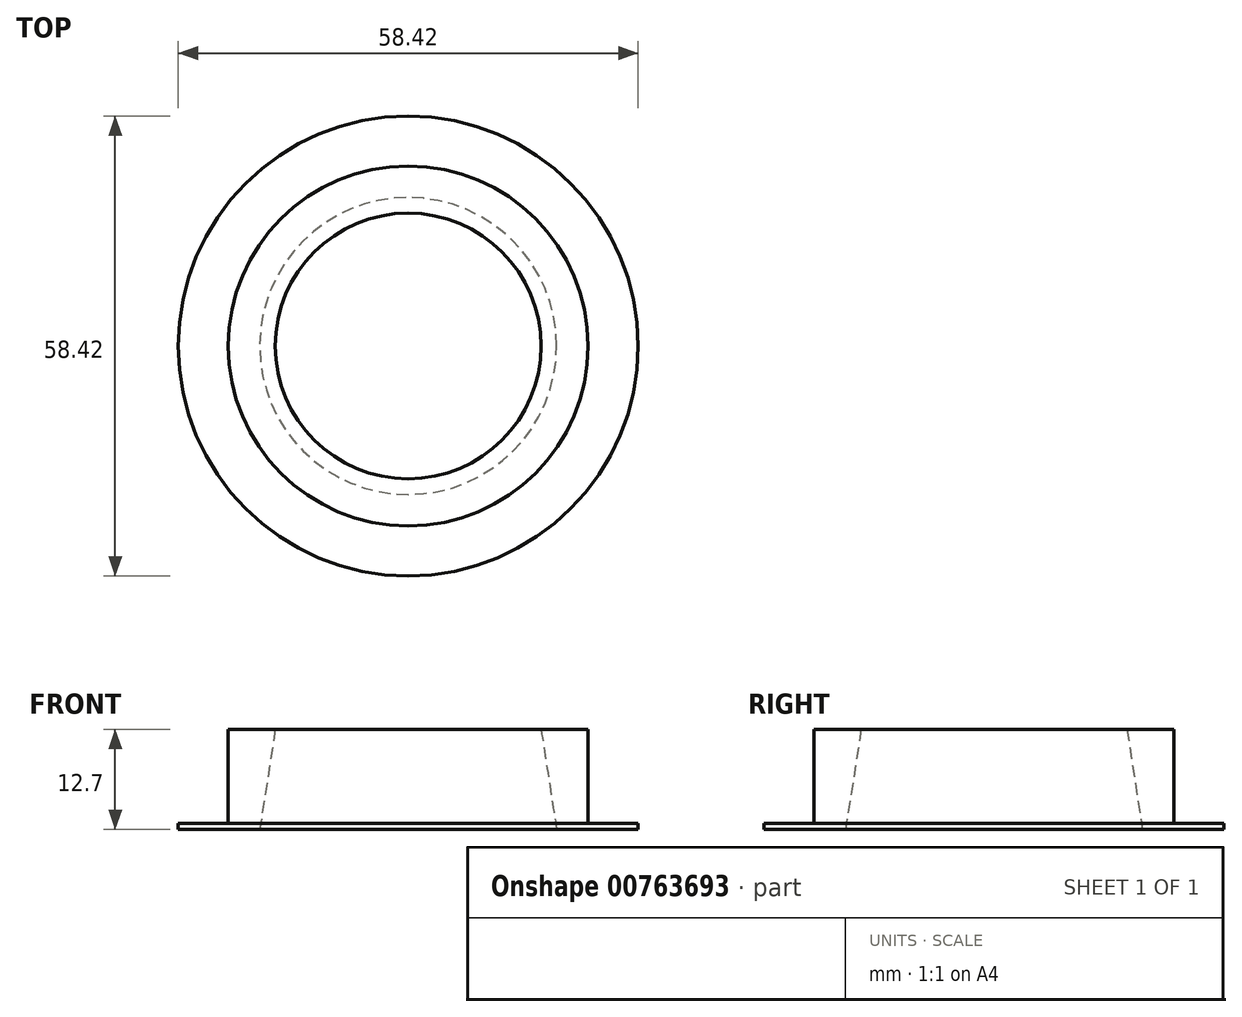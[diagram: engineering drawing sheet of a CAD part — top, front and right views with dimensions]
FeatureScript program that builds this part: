
annotation { "Feature Type Name" : "Feature", "Feature Type Description" : "" }
export const myFeature = defineFeature(function(context is Context, id is Id, definition is map)
    precondition{}
    {
        {
            var Q0;
            Q0=qCreatedBy(makeId("Top.planeOp"),FACE);
            var sketch = newSketch(context, id + "F0", { "sketchPlane" : qUnion([Q0])});
            skCircle(sketch, "E0", {"center": v(0, 0) * mm, "radius": 29.21 * mm});
            skSolve(sketch);
        }
        {
            var Q0;
            Q0 = qSketchRegion(id + "F0", true);
            extrude(context, id + "F1", {"entities" : qUnion([Q0]), "depth" : 0.76 * mm, "offsetDistance" : 25.4 * mm});
        }
        {
            var Q0;
            Q0=makeQuery(id+"F1.opExtrude","CAP_FACE",FACE,{"disambiguationData":[OSD([sQuery(id+"F0.wireOp",EDGE,"E0")])],"isStart":false});
            var sketch = newSketch(context, id + "F2", { "sketchPlane" : qUnion([Q0])});
            skCircle(sketch, "E1", {"center": v(0, 0) * mm, "radius": 22.86 * mm});
            skSolve(sketch);
        }
        {
            var Q0;
            Q0=makeQuery(id+"F2.imprint","IMPRINT",FACE,{"disambiguationData":[TD([[makeQuery(id+"F2.imprint","IMPRINT",EDGE,{"derivedFrom":sQuery(id+"F2.wireOp",EDGE,"E1")}),1.0]])]});
            extrude(context, id + "F3", {"entities" : qUnion([Q0]), "operationType" : NewBodyOperationType.ADD, "depth" : 11.94 * mm, "offsetDistance" : 25.4 * mm});
        }
        {
            var Q0;
            Q0=qCreatedBy(makeId("Front.planeOp"),FACE);
            var sketch = newSketch(context, id + "F4", { "sketchPlane" : qUnion([Q0])});
            skLineSegment(sketch, "E2", {"start": v(0, 0) * mm, "end": v(18.86, 0) * mm});
            skLineSegment(sketch, "E3", {"start": v(18.86, 0) * mm, "end": v(18.86, 39.24) * mm, "construction": true});
            skLineSegment(sketch, "E4", {"start": v(18.86, 39.24) * mm, "end": v(12.75, 39.24) * mm, "construction": true});
            skLineSegment(sketch, "E5", {"start": v(12.75, 39.24) * mm, "end": v(18.86, 0) * mm});
            skLineSegment(sketch, "E6", {"start": v(0, 0) * mm, "end": v(0, 39.24) * mm});
            skLineSegment(sketch, "E7", {"start": v(0, 39.24) * mm, "end": v(12.75, 39.24) * mm});
            skSolve(sketch);
        }
        {
            var Q0;
            Q0=makeQuery(id+"F4.imprint","IMPRINT",FACE,{"disambiguationData":[TD([[makeQuery(id+"F4.imprint","IMPRINT",EDGE,{"derivedFrom":sQuery(id+"F4.wireOp",EDGE,"E2")}),1.0]])]});
            var Q1;
            Q1=sQuery(id+"F4.wireOp",EDGE,"E6");
            revolve(context, id + "F5", {"operationType" : NewBodyOperationType.REMOVE, "surfaceOperationType" : NewSurfaceOperationType.NEW, "entities" : qUnion([Q0]), "axis" : qUnion([Q1]), "revolveType" : RevolveType.FULL, "oppositeDirection" : true});
        }
    });
